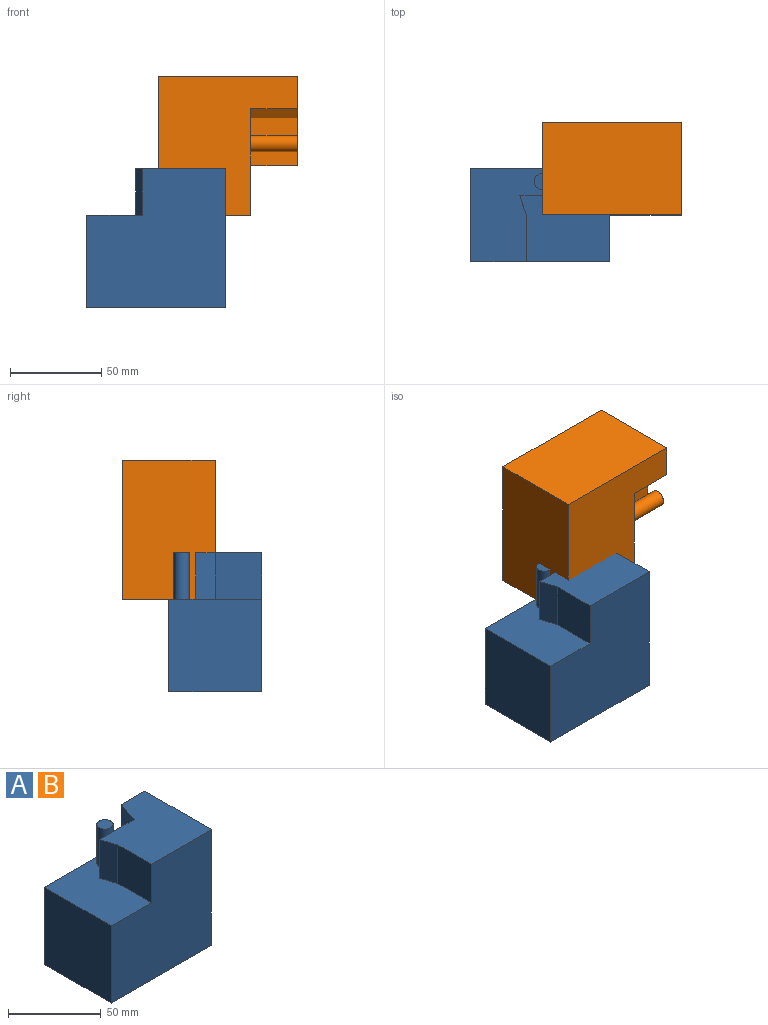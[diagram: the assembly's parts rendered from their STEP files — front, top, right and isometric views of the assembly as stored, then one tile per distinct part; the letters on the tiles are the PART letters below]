
ASSEMBLY  parts=2 mates=1
PART A: 13 faces, bbox 76.2x50.8x76.2 mm
  f0: plane 58.25x50.8mm, normal (0,0,1), area 1842.7mm2, adj f1,f4,f5,f7,f8,f9,f11,f12
  f1: plane 50.8x50.8mm, normal (-1,0,0), area 2580.6mm2, adj f0,f2,f4,f12
  f2: plane 76.2x50.8mm, normal (0,0,-1), area 3871mm2, adj f1,f3,f4,f12
  f3: plane 76.2x50.8mm, normal (1,0,0), area 3871mm2, adj f2,f4,f10,f12
  f4: plane 76.2x76.2mm, normal (0,1,0), area 4326.9mm2, adj f0,f1,f2,f3,f7,f10
  f5: cylinder r=4.4mm len=25.4mm, axis (0,0,-1), area 701.6mm2, adj f0,f6
  f6: plane 8.79x8.79mm, normal (0,0,1), area 60.7mm2, adj f5
  f7: plane 25.4x14.77mm, normal (-0.95,0.31,0), area 394.7mm2, adj f0,f4,f8,f10
  f8: plane 26.45x25.4mm, normal (0,1,0), area 671.8mm2, adj f0,f7,f9,f10
  f9: plane 25.4x10.63mm, normal (-0.95,-0.31,0), area 284.2mm2, adj f0,f8,f10,f11
  f10: plane 50.8x49.24mm, normal (0,0,1), area 1967.6mm2, adj f3,f4,f7,f8,f9,f11,f12
  f11: plane 25.4x25.4mm, normal (-1,0,0), area 645.2mm2, adj f0,f9,f10,f12
  f12: plane 76.2x76.2mm, normal (0,-1,0), area 5032.9mm2, adj f0,f1,f2,f3,f10,f11
PART B: same geometry as A
PLACE A t=(-64.64,1.87,-18.66)mm fixed
PLACE B rot(axis=(0.71,0,0.71),180deg) t=(-25.52,-23.53,32.14)mm
MATE planar B.f1 <-> A.f0  axis (0,0,-1) through (-0.12,1.87,32.14)mm
